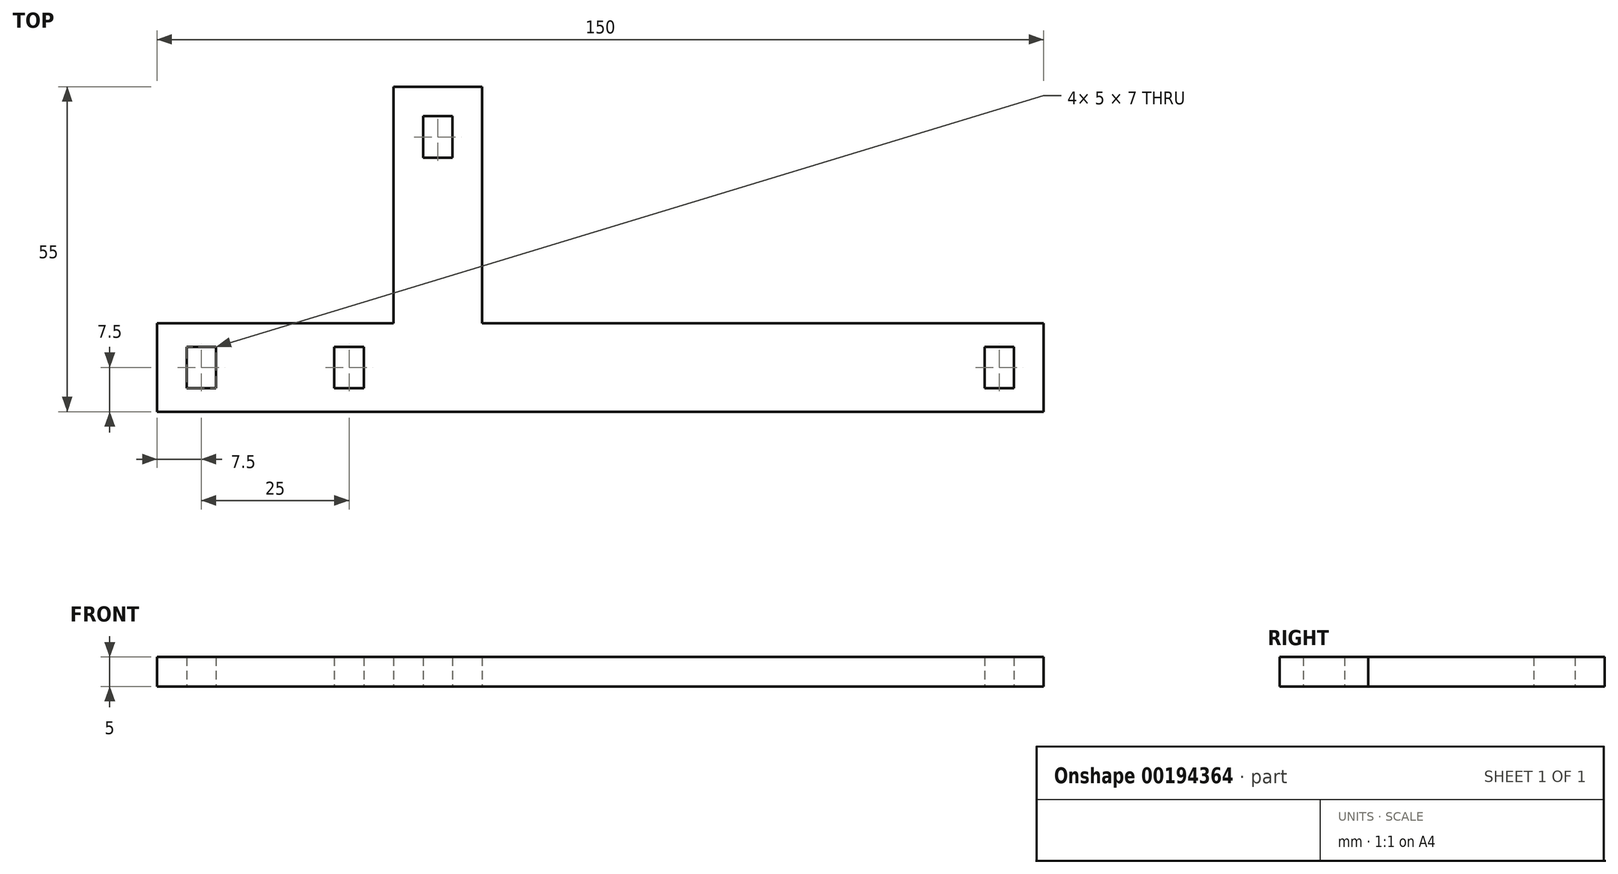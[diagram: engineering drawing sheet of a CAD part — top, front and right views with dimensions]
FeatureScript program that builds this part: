
annotation { "Feature Type Name" : "Feature", "Feature Type Description" : "" }
export const myFeature = defineFeature(function(context is Context, id is Id, definition is map)
    precondition{}
    {
        {
            var Q0;
            Q0=qCreatedBy(makeId("Top.planeOp"),FACE);
            var sketch = newSketch(context, id + "F0", { "sketchPlane" : qUnion([Q0])});
            skLineSegment(sketch, "E0", {"start": v(0, 0) * mm, "end": v(0, 15) * mm, "construction": true});
            skLineSegment(sketch, "E1", {"start": v(0, 15) * mm, "end": v(150, 15) * mm, "construction": true});
            skLineSegment(sketch, "E2", {"start": v(150, 15) * mm, "end": v(150, 0) * mm});
            skLineSegment(sketch, "E3", {"start": v(150, 0) * mm, "end": v(55, 0) * mm});
            skLineSegment(sketch, "E4", {"start": v(55, 0) * mm, "end": v(55, -40) * mm});
            skLineSegment(sketch, "E5", {"start": v(55, -40) * mm, "end": v(40, -40) * mm});
            skLineSegment(sketch, "E6", {"start": v(40, -40) * mm, "end": v(40, 0) * mm, "construction": true});
            skLineSegment(sketch, "E7", {"start": v(40, 0) * mm, "end": v(0, 0) * mm, "construction": true});
            skLineSegment(sketch, "E8", {"start": v(0, 7.5) * mm, "end": v(150, 7.5) * mm, "construction": true});
            skLineSegment(sketch, "E9", {"start": v(47.5, -40) * mm, "end": v(47.5, 7.5) * mm, "construction": true});
            skLineSegment(sketch, "E10.bottom", {"start": v(5, 11) * mm, "end": v(10, 11) * mm, "construction": true});
            skLineSegment(sketch, "E10.top", {"start": v(5, 4) * mm, "end": v(10, 4) * mm, "construction": true});
            skLineSegment(sketch, "E10.left", {"start": v(5, 11) * mm, "end": v(5, 4) * mm, "construction": true});
            skLineSegment(sketch, "E10.right", {"start": v(10, 11) * mm, "end": v(10, 4) * mm, "construction": true});
            skPoint(sketch, "E10.middle", {"position": v(7.5, 7.5) * mm});
            skLineSegment(sketch, "E11.bottom", {"start": v(30, 11) * mm, "end": v(35, 11) * mm, "construction": true});
            skLineSegment(sketch, "E11.top", {"start": v(30, 4) * mm, "end": v(35, 4) * mm, "construction": true});
            skLineSegment(sketch, "E11.left", {"start": v(30, 11) * mm, "end": v(30, 4) * mm, "construction": true});
            skLineSegment(sketch, "E11.right", {"start": v(35, 11) * mm, "end": v(35, 4) * mm, "construction": true});
            skPoint(sketch, "E11.middle", {"position": v(32.5, 7.5) * mm});
            skLineSegment(sketch, "E12.bottom", {"start": v(50, -28) * mm, "end": v(45, -28) * mm, "construction": true});
            skLineSegment(sketch, "E12.top", {"start": v(50, -35) * mm, "end": v(45, -35) * mm, "construction": true});
            skLineSegment(sketch, "E12.left", {"start": v(50, -28) * mm, "end": v(50, -35) * mm, "construction": true});
            skLineSegment(sketch, "E12.right", {"start": v(45, -28) * mm, "end": v(45, -35) * mm, "construction": true});
            skPoint(sketch, "E12.middle", {"position": v(47.5, -31.5) * mm});
            skLineSegment(sketch, "E13.bottom", {"start": v(140, 4) * mm, "end": v(145, 4) * mm, "construction": true});
            skLineSegment(sketch, "E13.top", {"start": v(140, 11) * mm, "end": v(145, 11) * mm, "construction": true});
            skLineSegment(sketch, "E13.left", {"start": v(140, 4) * mm, "end": v(140, 11) * mm, "construction": true});
            skLineSegment(sketch, "E13.right", {"start": v(145, 4) * mm, "end": v(145, 11) * mm, "construction": true});
            skPoint(sketch, "E13.middle", {"position": v(142.5, 7.5) * mm});
            skLineSegment(sketch, "E14", {"start": v(-22.6, -52.5) * mm, "end": v(153.2, -52.5) * mm, "construction": true});
            skLineSegment(sketch, "E15.MirrorCS", {"start": v(5, -109) * mm, "end": v(10, -109) * mm});
            skLineSegment(sketch, "E16.MirrorCS", {"start": v(5, -116) * mm, "end": v(5, -109) * mm});
            skLineSegment(sketch, "E17.MirrorCS", {"start": v(145, -109) * mm, "end": v(145, -116) * mm});
            skLineSegment(sketch, "E18.MirrorCS", {"start": v(140, -109) * mm, "end": v(145, -109) * mm});
            skLineSegment(sketch, "E19.MirrorCS", {"start": v(140, -109) * mm, "end": v(140, -116) * mm});
            skLineSegment(sketch, "E20.MirrorCS", {"start": v(35, -116) * mm, "end": v(35, -109) * mm});
            skLineSegment(sketch, "E21.MirrorCS", {"start": v(30, -109) * mm, "end": v(35, -109) * mm});
            skLineSegment(sketch, "E22.MirrorCS", {"start": v(30, -116) * mm, "end": v(30, -109) * mm});
            skLineSegment(sketch, "E23.MirrorCS", {"start": v(140, -116) * mm, "end": v(145, -116) * mm});
            skLineSegment(sketch, "E24.MirrorCS", {"start": v(50, -77) * mm, "end": v(45, -77) * mm});
            skLineSegment(sketch, "E25.MirrorCS", {"start": v(45, -77) * mm, "end": v(45, -70) * mm});
            skLineSegment(sketch, "E26.MirrorCS", {"start": v(50, -70) * mm, "end": v(45, -70) * mm});
            skLineSegment(sketch, "E27.MirrorCS", {"start": v(10, -116) * mm, "end": v(10, -109) * mm});
            skLineSegment(sketch, "E28.MirrorCS", {"start": v(30, -116) * mm, "end": v(35, -116) * mm});
            skLineSegment(sketch, "E29.MirrorCS", {"start": v(0, -105) * mm, "end": v(0, -120) * mm});
            skLineSegment(sketch, "E30.MirrorCS", {"start": v(150, -120) * mm, "end": v(150, -105) * mm});
            skLineSegment(sketch, "E31.MirrorCS", {"start": v(55, -65) * mm, "end": v(40, -65) * mm});
            skLineSegment(sketch, "E32.MirrorCS", {"start": v(5, -116) * mm, "end": v(10, -116) * mm});
            skLineSegment(sketch, "E33.MirrorCS", {"start": v(50, -77) * mm, "end": v(50, -70) * mm});
            skLineSegment(sketch, "E34.MirrorCS", {"start": v(40, -65) * mm, "end": v(40, -105) * mm});
            skLineSegment(sketch, "E35.MirrorCS", {"start": v(0, -112.5) * mm, "end": v(150, -112.5) * mm, "construction": true});
            skLineSegment(sketch, "E36.MirrorCS", {"start": v(47.5, -65) * mm, "end": v(47.5, -112.5) * mm, "construction": true});
            skPoint(sketch, "E37.MirrorP", {"position": v(142.5, -112.5) * mm});
            skPoint(sketch, "E38.MirrorP", {"position": v(47.5, -73.5) * mm});
            skPoint(sketch, "E39.MirrorP", {"position": v(7.5, -112.5) * mm});
            skLineSegment(sketch, "E40.MirrorCS", {"start": v(0, -120) * mm, "end": v(150, -120) * mm});
            skLineSegment(sketch, "E41.MirrorCS", {"start": v(150, -105) * mm, "end": v(55, -105) * mm});
            skLineSegment(sketch, "E42.MirrorCS", {"start": v(55, -105) * mm, "end": v(55, -65) * mm});
            skLineSegment(sketch, "E43.MirrorCS", {"start": v(40, -105) * mm, "end": v(0, -105) * mm});
            skPoint(sketch, "E44.MirrorP", {"position": v(32.5, -112.5) * mm});
            skSolve(sketch);
        }
        {
            var Q0;
            Q0=makeQuery(id+"F0.imprint","IMPRINT",FACE,{"disambiguationData":[TD([[makeQuery(id+"F0.imprint","IMPRINT",EDGE,{"derivedFrom":sQuery(id+"F0.wireOp",EDGE,"E15.MirrorCS")}),1.0]])]});
            extrude(context, id + "F1", {"entities" : qUnion([Q0]), "depth" : 5 * mm});
        }
    });
